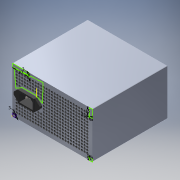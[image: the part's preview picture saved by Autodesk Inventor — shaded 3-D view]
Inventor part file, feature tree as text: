
AUTODESK INVENTOR PART (.ipt)
format: ipt  version: 2017 (Build 210142000, 142)  size: 1,044,480 bytes
history: mixed  units: mm
features: sketch x3, extrude x3, fillet x1, imported_body x1
ambient origin geometry x8: Origin, YZ Plane, XZ Plane, XY Plane, X Axis, Y Axis, Z Axis, Center Point
bodies: Solid1 (imported_parasolid)
feature tree (8):
  sketch  "Sketch1"  dims[d0=6.0mm d1=5.0mm]
  extrude  "Extrusion1"  Depth=5.0mm
  extrude  "Extrusion2"  Depth=6.0mm
  extrude  "Extrusion3"  Depth=10.0mm
  sketch  "Sketch2"  dims[d2=3.0mm d3=6.0mm]
  sketch  "Sketch3"  dims[d4=17.0mm d5=30.0mm d6=6.0mm d7=6.0mm d8=5.0mm d9=3.0mm d10=3.0mm d11=3.0mm d12=10.0mm d13=0.0mm d14=10.0mm d15=0.0mm d16=10.0mm d17=0.0mm]
  fillet  "Fillet3"  Radius=6.0mm
  imported_body  NMx_Import_Brep_tag  [imported B-rep: ~32 faces, bbox_mm=[149.86, 140.462, 85.725]]
